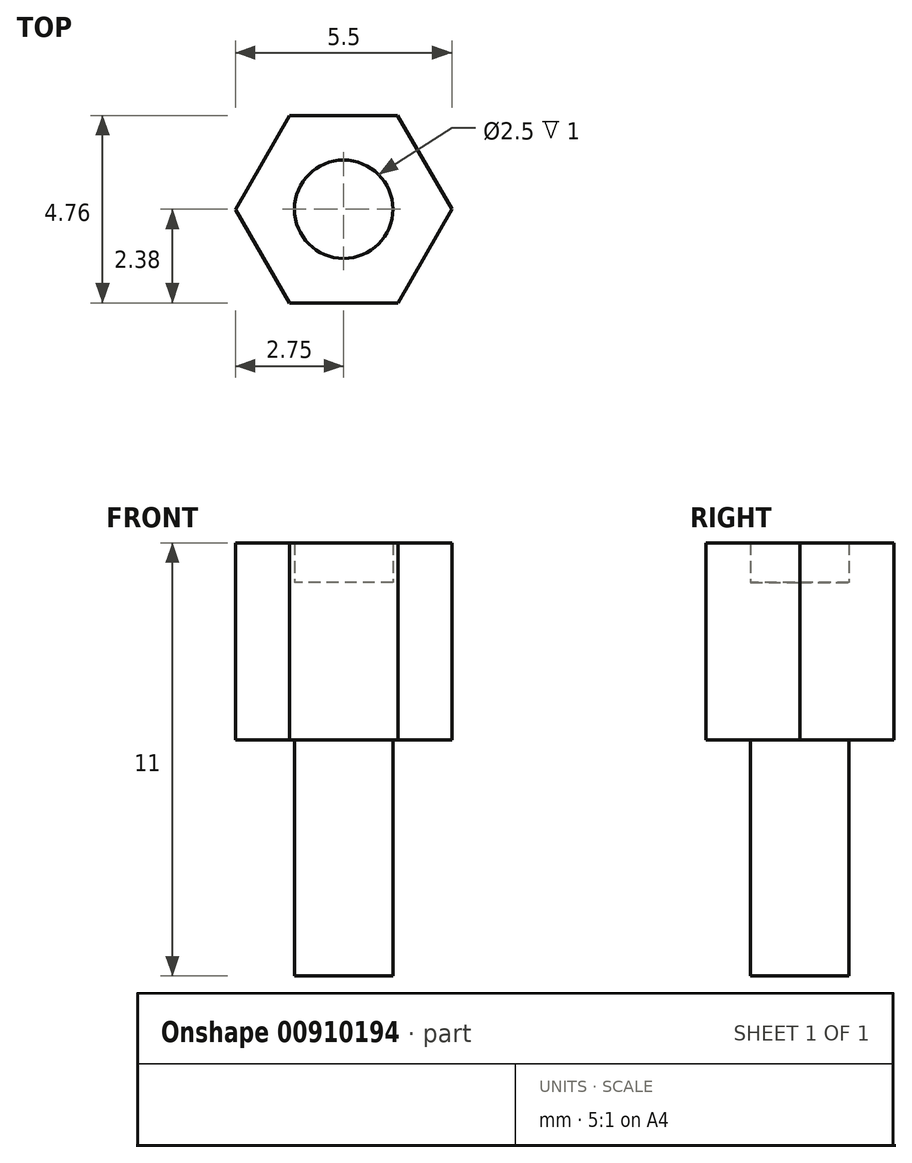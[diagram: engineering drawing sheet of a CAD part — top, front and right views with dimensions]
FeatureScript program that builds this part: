
annotation { "Feature Type Name" : "Feature", "Feature Type Description" : "" }
export const myFeature = defineFeature(function(context is Context, id is Id, definition is map)
    precondition{}
    {
        {
            var Q0;
            Q0=qCreatedBy(makeId("Top.planeOp"),FACE);
            var sketch = newSketch(context, id + "F0", { "sketchPlane" : qUnion([Q0])});
            skCircle(sketch, "E0.cCircle", {"center": v(0, 0) * mm, "radius": 2.38 * mm, "construction": true});
            skLineSegment(sketch, "E0.0", {"start": v(2.75, 0) * mm, "end": v(1.38, -2.38) * mm});
            skLineSegment(sketch, "E0.1", {"start": v(1.38, -2.38) * mm, "end": v(-1.37, -2.38) * mm});
            skLineSegment(sketch, "E0.2", {"start": v(-1.37, -2.38) * mm, "end": v(-2.75, 0) * mm});
            skLineSegment(sketch, "E0.3", {"start": v(-2.75, 0) * mm, "end": v(-1.38, 2.38) * mm});
            skLineSegment(sketch, "E0.4", {"start": v(-1.38, 2.38) * mm, "end": v(1.37, 2.38) * mm});
            skLineSegment(sketch, "E0.5", {"start": v(1.37, 2.38) * mm, "end": v(2.75, 0) * mm});
            skPoint(sketch, "E0.0.midPoint", {"position": v(2.06, -1.19) * mm});
            skSolve(sketch);
        }
        {
            var Q0;
            Q0 = qSketchRegion(id + "F0", true);
            extrude(context, id + "F1", {"entities" : qUnion([Q0]), "depth" : 5 * mm, "offsetDistance" : 25 * mm});
        }
        {
            var Q0;
            Q0=qCreatedBy(makeId("Top.planeOp"),FACE);
            var sketch = newSketch(context, id + "F2", { "sketchPlane" : qUnion([Q0])});
            skCircle(sketch, "E1", {"center": v(0, 0) * mm, "radius": 1.25 * mm});
            skSolve(sketch);
        }
        {
            var Q0;
            Q0 = qSketchRegion(id + "F2", true);
            extrude(context, id + "F3", {"entities" : qUnion([Q0]), "operationType" : NewBodyOperationType.ADD, "oppositeDirection" : true, "depth" : 6 * mm, "offsetDistance" : 25 * mm});
        }
        {
            var Q0;
            Q0=qCreatedBy(makeId("Top.planeOp"),FACE);
            cPlane(context, id + "F4", {"entities" : qUnion([Q0]), "cplaneType" : CPlaneType.OFFSET, "offset" : 4 * mm, "width" : 150 * mm, "height" : 150 * mm});
        }
        {
            var Q0;
            Q0=qCreatedBy(id+"F4.planeOp",FACE);
            var sketch = newSketch(context, id + "F5", { "sketchPlane" : qUnion([Q0])});
            skCircle(sketch, "E2", {"center": v(0, 0) * mm, "radius": 1.25 * mm});
            skSolve(sketch);
        }
        {
            var Q0;
            Q0 = qSketchRegion(id + "F5", true);
            extrude(context, id + "F6", {"entities" : qUnion([Q0]), "operationType" : NewBodyOperationType.REMOVE, "depth" : 7 * mm, "offsetDistance" : 25 * mm});
        }
    });
